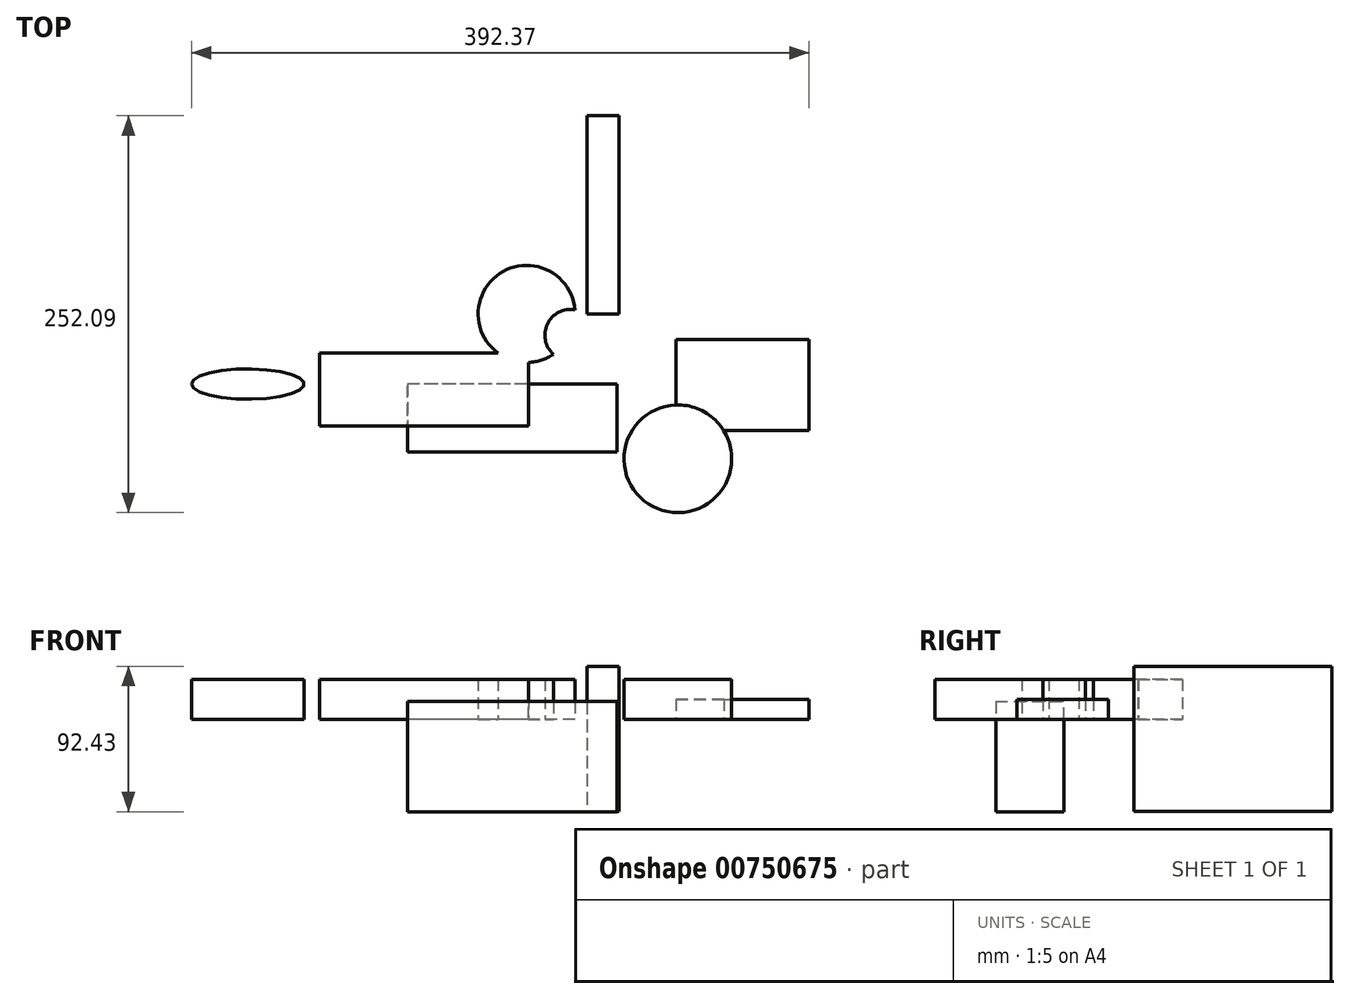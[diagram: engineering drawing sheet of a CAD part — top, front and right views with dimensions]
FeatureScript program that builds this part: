
annotation { "Feature Type Name" : "Feature", "Feature Type Description" : "" }
export const myFeature = defineFeature(function(context is Context, id is Id, definition is map)
    precondition{}
    {
        {
            var Q0;
            Q0=qCreatedBy(makeId("Front.planeOp"),FACE);
            var sketch = newSketch(context, id + "F0", { "sketchPlane" : qUnion([Q0])});
            skLineSegment(sketch, "E0.bottom", {"start": v(19.05, 11.23) * mm, "end": v(-114.06, 11.23) * mm});
            skLineSegment(sketch, "E0.top", {"start": v(19.05, -58.74) * mm, "end": v(-114.06, -58.74) * mm});
            skLineSegment(sketch, "E0.left", {"start": v(19.05, 11.23) * mm, "end": v(19.05, -58.74) * mm});
            skLineSegment(sketch, "E0.right", {"start": v(-114.06, 11.23) * mm, "end": v(-114.06, -58.74) * mm});
            skSolve(sketch);
        }
        {
            var Q0;
            Q0=makeQuery(id+"F0.imprint","IMPRINT",FACE,{"disambiguationData":[TD([[makeQuery(id+"F0.imprint","IMPRINT",EDGE,{"derivedFrom":sQuery(id+"F0.wireOp",EDGE,"E0.bottom")}),1.0]])]});
            extrude(context, id + "F1", {"entities" : qUnion([Q0]), "depth" : 43.18 * mm, "offsetDistance" : 25.4 * mm});
        }
        {
            var Q0;
            Q0=qCreatedBy(makeId("Top.planeOp"),FACE);
            var sketch = newSketch(context, id + "F2", { "sketchPlane" : qUnion([Q0])});
            skLineSegment(sketch, "E1.bottom", {"start": v(56.6, 28.4) * mm, "end": v(141.14, 28.4) * mm});
            skLineSegment(sketch, "E1.top", {"start": v(56.6, -29.62) * mm, "end": v(141.14, -29.62) * mm});
            skLineSegment(sketch, "E1.left", {"start": v(56.6, 28.4) * mm, "end": v(56.6, -29.62) * mm});
            skLineSegment(sketch, "E1.right", {"start": v(141.14, 28.4) * mm, "end": v(141.14, -29.62) * mm});
            skSolve(sketch);
        }
        {
            var Q0;
            Q0=makeQuery(id+"F2.imprint","IMPRINT",FACE,{"disambiguationData":[TD([[makeQuery(id+"F2.imprint","IMPRINT",EDGE,{"derivedFrom":sQuery(id+"F2.wireOp",EDGE,"E1.bottom")}),-1.0]])]});
            extrude(context, id + "F3", {"entities" : qUnion([Q0]), "depth" : 12.7 * mm, "offsetDistance" : 25.4 * mm});
        }
        {
            var Q0;
            Q0=qCreatedBy(makeId("Right.planeOp"),FACE);
            var sketch = newSketch(context, id + "F4", { "sketchPlane" : qUnion([Q0])});
            skLineSegment(sketch, "E2.bottom", {"start": v(44.5, 33.69) * mm, "end": v(170.37, 33.69) * mm});
            skLineSegment(sketch, "E2.top", {"start": v(44.5, -58.5) * mm, "end": v(170.37, -58.5) * mm});
            skLineSegment(sketch, "E2.left", {"start": v(44.5, 33.69) * mm, "end": v(44.5, -58.5) * mm});
            skLineSegment(sketch, "E2.right", {"start": v(170.37, 33.69) * mm, "end": v(170.37, -58.5) * mm});
            skSolve(sketch);
        }
        {
            var Q0;
            Q0=makeQuery(id+"F4.imprint","IMPRINT",FACE,{"disambiguationData":[TD([[makeQuery(id+"F4.imprint","IMPRINT",EDGE,{"derivedFrom":sQuery(id+"F4.wireOp",EDGE,"E2.bottom")}),-1.0]])]});
            extrude(context, id + "F5", {"entities" : qUnion([Q0]), "depth" : 20.32 * mm, "offsetDistance" : 25.4 * mm});
        }
        {
            var Q0;
            Q0=qCreatedBy(makeId("Top.planeOp"),FACE);
            var sketch = newSketch(context, id + "F6", { "sketchPlane" : qUnion([Q0])});
            skLineSegment(sketch, "E3.bottom", {"start": v(-37.18, 19.65) * mm, "end": v(-169.87, 19.65) * mm});
            skLineSegment(sketch, "E3.top", {"start": v(-37.18, -26.7) * mm, "end": v(-169.87, -26.7) * mm});
            skLineSegment(sketch, "E3.left", {"start": v(-37.18, 19.65) * mm, "end": v(-37.18, -26.7) * mm});
            skLineSegment(sketch, "E3.right", {"start": v(-169.87, 19.65) * mm, "end": v(-169.87, -26.7) * mm});
            skSolve(sketch);
        }
        {
            var Q0;
            Q0=makeQuery(id+"F6.imprint","IMPRINT",FACE,{"disambiguationData":[TD([[makeQuery(id+"F6.imprint","IMPRINT",EDGE,{"derivedFrom":sQuery(id+"F6.wireOp",EDGE,"E3.bottom")}),1.0]])]});
            extrude(context, id + "F7", {"entities" : qUnion([Q0]), "operationType" : NewBodyOperationType.ADD, "depth" : 25.4 * mm, "offsetDistance" : 25.4 * mm});
        }
        {
            var Q0;
            Q0=qCreatedBy(makeId("Top.planeOp"),FACE);
            var sketch = newSketch(context, id + "F8", { "sketchPlane" : qUnion([Q0])});
            skCircle(sketch, "E4", {"center": v(-38.28, 44.54) * mm, "radius": 30.81 * mm});
            skCircle(sketch, "E5", {"center": v(-10.54, 31.1) * mm, "radius": 16.24 * mm});
            skSolve(sketch);
        }
        {
            var Q0;
            {var subQ0=sQuery(id+"F8.wireOp",EDGE,"E5");var subQ1=sQuery(id+"F8.wireOp",EDGE,"E4");var subQ2=makeQuery(id+"F8.imprint","INTERSECT",VERTEX,{"disambiguationData":[OD(0.0)],"derivedFrom":[subQ1,subQ0]});Q0=makeQuery(id+"F8.imprint","IMPRINT",FACE,{"disambiguationData":[TD([[makeQuery(id+"F8.imprint","IMPRINT",EDGE,{"disambiguationData":[TD([[subQ2,1.0]])],"derivedFrom":subQ1}),1.0]])]});}
            extrude(context, id + "F9", {"entities" : qUnion([Q0]), "operationType" : NewBodyOperationType.ADD, "depth" : 25.4 * mm, "offsetDistance" : 25.4 * mm});
        }
        {
            var Q0;
            Q0=qCreatedBy(makeId("Top.planeOp"),FACE);
            var sketch = newSketch(context, id + "F10", { "sketchPlane" : qUnion([Q0])});
            skCircle(sketch, "E6", {"center": v(57.7, -47.5) * mm, "radius": 34.22 * mm});
            skSolve(sketch);
        }
        {
            var Q0;
            Q0=makeQuery(id+"F10.imprint","IMPRINT",FACE,{"disambiguationData":[TD([[makeQuery(id+"F10.imprint","IMPRINT",EDGE,{"derivedFrom":sQuery(id+"F10.wireOp",EDGE,"E6")}),1.0]])]});
            extrude(context, id + "F11", {"entities" : qUnion([Q0]), "operationType" : NewBodyOperationType.ADD, "depth" : 25.4 * mm, "offsetDistance" : 25.4 * mm});
        }
        {
            var Q0;
            Q0=qCreatedBy(makeId("Top.planeOp"),FACE);
            var sketch = newSketch(context, id + "F12", { "sketchPlane" : qUnion([Q0])});
            skEllipse(sketch, "E7", {"center": v(-215.44, 0) * mm, "majorRadius": 35.8 * mm, "minorRadius": 9.6 * mm, "majorAxis": v(-1, 0)});
            skSolve(sketch);
        }
        {
            var Q0;
            Q0=makeQuery(id+"F12.imprint","IMPRINT",FACE,{"disambiguationData":[TD([[makeQuery(id+"F12.imprint","IMPRINT",EDGE,{"derivedFrom":sQuery(id+"F12.wireOp",EDGE,"E7")}),1.0]])]});
            extrude(context, id + "F13", {"entities" : qUnion([Q0]), "depth" : 25.4 * mm, "offsetDistance" : 25.4 * mm});
        }
    });
